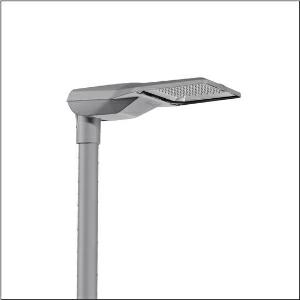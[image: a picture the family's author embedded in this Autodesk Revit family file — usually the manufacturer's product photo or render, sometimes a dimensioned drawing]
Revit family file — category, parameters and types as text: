
# Revit family: streetlight_sl_21_midi___st0_8a_5xe7c63a08lb_8ff2
name_source: partatom
category: Lighting Fixtures
units: mm (PartAtom-declared; Revit-internal decimal feet)

## family parameters
Cut with Voids When Loaded = No
Host = Face
Light Source = No
Part Type = Normal
Room Calculation Point = No
Round Connector Dimension = Use Diameter
Shared = No

## types (1)
- --- (1 x LED, 12860 lm, 98.3 W, 2700K)
    Apparent Load = 98 VA
    CIE Flux Codes = 38 75 97 100 100
    Color Rendering = 70
    Color Temperature = 2700K
    Default Elevation = 1800 mm
    Description = Streetlight SL 21 midi, mast luminaire, primary light control with lens, of PMMA, primary optical cover: cover, of toughened safety glass, transparent, light distribution: ST0.8a, light emission: direct distribution, primary light characteristic: asymmetric, installation type: post-top, side-entry, LED, 3G 1.5mm², High Power LED, rated luminous flux: 12.860lm, luminous efficacy: 131lm/W, light colour: 727, colour temperature: 2700K, control: overheat protection, constant luminous flux control, time-dependent luminous flux control, flexible luminous flux parameterisation, mains connection: 220..240V, AC, 50/60Hz, connection cable pre-assembled, cable length: 10,5m, wiring characteristics: H07RN-F, start of lifetime: 98W, end of service life: 101W, reduction: 44W, luminaire housing, of diecast aluminium, powder-coated, Siteco® metallic grey (DB 702S), corrosivity category C5 mid according to DIN EN ISO 12944, please order mast flange separately, inclination adjustable: 0°, 5°, 10°, 15°, sealing non-destructively replaceable, multi-level sealing system, length: 644mm, width: 335mm, height: 110mm, mast flange for spigot size: 42mm (side-entry): 5XC10008XM4, 60/48mm (side-entry/post-top): 5XC10108XM2, 76/60mm (side-entry/post-top): 5XC10108XM1, protection rating (complete): IP66, insulation class (complete): insulation class II (safety insulation), certification: CE, ENEC, ENEC+, VDE, impact resistance: IK09, permissible operating ambient temperature for outdoor applications: -40..+50°C, standard-compliant lighting for roads and squares, packaging unit: 1 piece

Light Distribution: ST0.8a
    Height = 111 mm
    Lamp = 1 x LED
    Lamp Light Flux = 12860 lm
    Lamp Power = 98.3 W
    Lamp count = 1
    Length = 644 mm
    Luminous efficacy = 131 lm/W
    Manufacturer = Siteco
    ModVariant = No
    Model = 5XE7C63A08LB
    Number of Poles = 1
    OnlyDefault = Yes
    Power Factor = 1
    Product Name = Streetlight SL 21 midi | ST0.8a
    Product group = mast luminaire | pylon top
    ProductGroupID = 6100
    Protection Class = Protection class II
    Protection Degree = IP 66
    RLX_Detail_Level = 1
    RLX_Emergency_Light_Flux = 0 lm
    RLX_Emergency_Type = 0
    RLX_Emergency_Type_DB = No
    RlxData = <blob elided: 90813 chars, md5=1dc6ed3e>
    Socket = socket
    Standby Power = 0 W
    System Light Flux = 12860 lm
    System Power = 98 W
    Type Comments = factory setting: luminous flux: 100 % | Output Level: 100 % | 1020 mA
    Type Image = l_1004298.jpg
    URL = http://relux.com
    VarID = @adj_137433
    Voltage = 0 V
    Weight = 0.00 kg
    Width = 336 mm

## geometry (parser evidence)
native form markers: Blend x4, Sweep x13
no freeform markers — native parametric forms only
